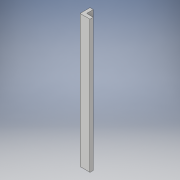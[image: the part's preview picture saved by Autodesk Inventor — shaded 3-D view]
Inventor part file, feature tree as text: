
AUTODESK INVENTOR PART (.ipt)
format: ipt  version: 2017 (Build 210142000, 142)  size: 114,176 bytes
history: native  units: in
note: dims shown in document units (in); Inventor stores cm internally (conversion verified against a paired STEP export)
features: extrude x3, sketch x3
ambient origin geometry x8: Origin, YZ Plane, XZ Plane, XY Plane, X Axis, Y Axis, Z Axis, Center Point
bodies: Solid1 (feature_tree)
feature tree (6):
  extrude  "Extrusion1"  Depth=1.0in
  extrude  "Extrusion2"  Depth=2.0in TaperAngle=0.0deg
  extrude  "Extrusion4"  Depth=40.0in
  sketch  "Sketch1"  dims[d0=1.0in d1=1.0in]
  sketch  "Sketch2"  dims[d2=40.0in d3=0.0in d4=2.0in d5=0.0in]
  sketch  "Sketch4"  dims[d8=1.0in d9=40.0in d10=2.0in d11=0.0in]
